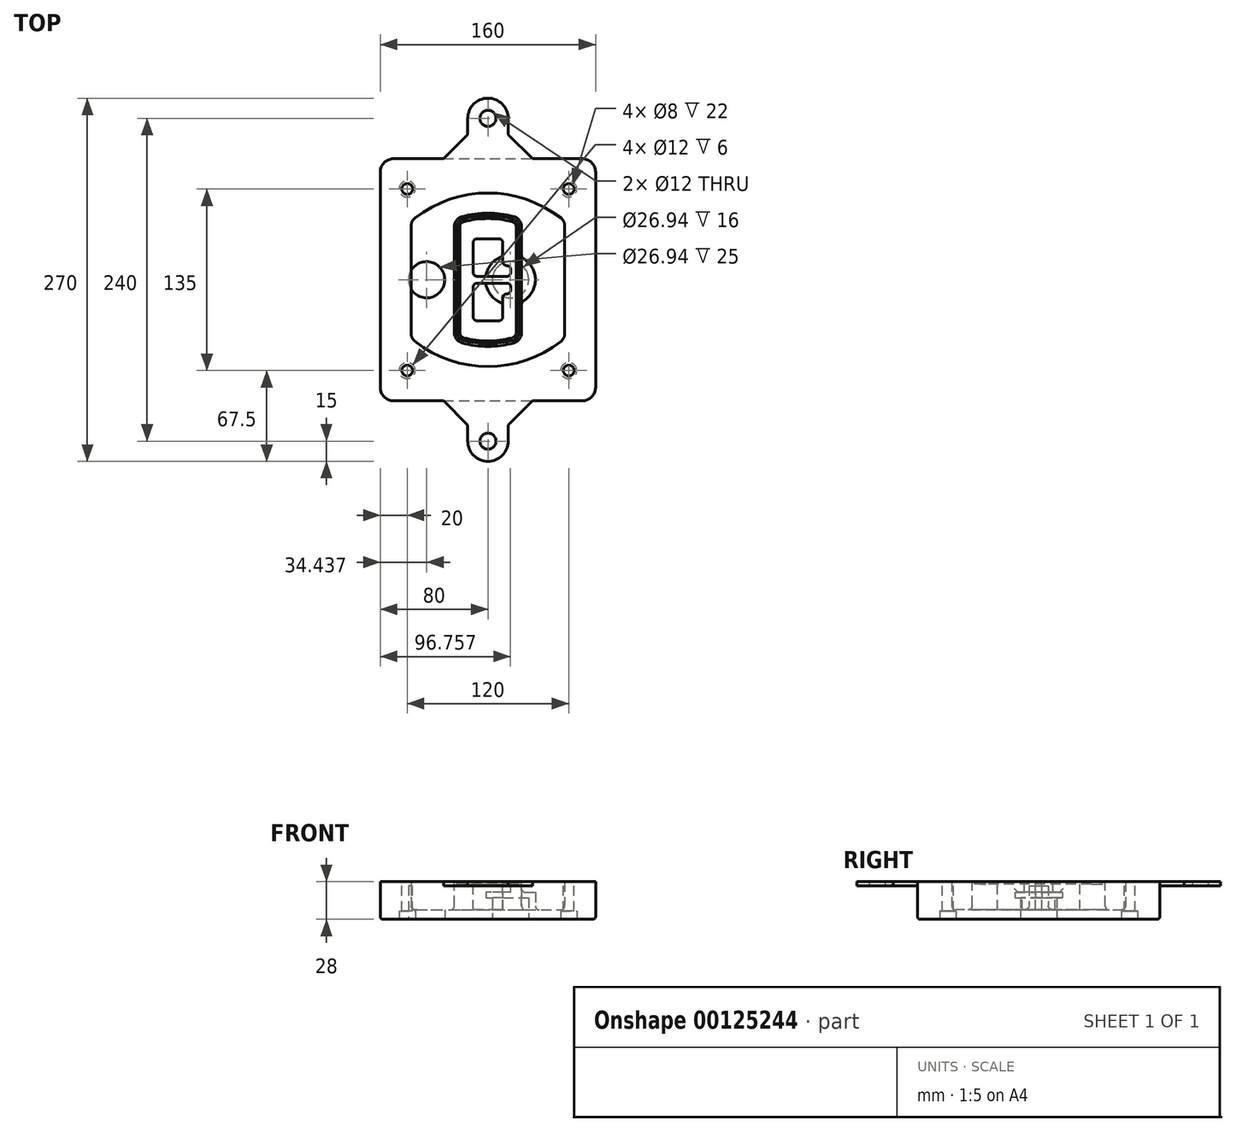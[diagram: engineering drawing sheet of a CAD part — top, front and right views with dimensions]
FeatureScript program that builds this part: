
annotation { "Feature Type Name" : "Feature", "Feature Type Description" : "" }
export const myFeature = defineFeature(function(context is Context, id is Id, definition is map)
    precondition{}
    {
        {
            var Q0;
            Q0=qCreatedBy(makeId("Top.planeOp"),FACE);
            var sketch = newSketch(context, id + "F0", { "sketchPlane" : qUnion([Q0])});
            skPoint(sketch, "E0.rect.middle", {"position": v(0, 0) * mm});
            skLineSegment(sketch, "E1.bottom", {"start": v(-70, -90) * mm, "end": v(70, -90) * mm});
            skLineSegment(sketch, "E1.top", {"start": v(-70, 90) * mm, "end": v(70, 90) * mm});
            skLineSegment(sketch, "E1.left", {"start": v(-80, -80) * mm, "end": v(-80, 80) * mm});
            skLineSegment(sketch, "E1.right", {"start": v(80, -80) * mm, "end": v(80, 80) * mm});
            skLineSegment(sketch, "E2", {"start": v(-80, 90) * mm, "end": v(80, -90) * mm, "construction": true});
            skLineSegment(sketch, "E3", {"start": v(80, 90) * mm, "end": v(-80, -90) * mm, "construction": true});
            skCircle(sketch, "E4", {"center": v(-60, 67.5) * mm, "radius": 4 * mm});
            skCircle(sketch, "E5", {"center": v(60, 67.5) * mm, "radius": 4 * mm});
            skCircle(sketch, "E6", {"center": v(60, -67.5) * mm, "radius": 4 * mm});
            skCircle(sketch, "E7", {"center": v(-60, -67.5) * mm, "radius": 4 * mm});
            skLineSegment(sketch, "E8", {"start": v(-60, 67.5) * mm, "end": v(60, 67.5) * mm, "construction": true});
            skLineSegment(sketch, "E9", {"start": v(60, 67.5) * mm, "end": v(60, -67.5) * mm, "construction": true});
            skLineSegment(sketch, "E10", {"start": v(60, -67.5) * mm, "end": v(-60, -67.5) * mm, "construction": true});
            skLineSegment(sketch, "E11", {"start": v(-60, -67.5) * mm, "end": v(-60, 67.5) * mm, "construction": true});
            skLineSegment(sketch, "E12", {"start": v(-60, 40.3) * mm, "end": v(-60, -40.3) * mm});
            skLineSegment(sketch, "E13", {"start": v(60, 40.3) * mm, "end": v(60, -40.3) * mm});
            skArc(sketch, "E14", {"start": v(56.15, 48.18) * mm, "mid": v(0, 67.5) * mm, "end": v(-56.15, 48.18) * mm});
            skArc(sketch, "E15", {"start": v(-56.15, -48.18) * mm, "mid": v(0, -67.5) * mm, "end": v(56.15, -48.18) * mm});
            skLineSegment(sketch, "E16", {"start": v(-60, 0) * mm, "end": v(60, 0) * mm, "construction": true});
            skPoint(sketch, "E17.visualSharp", {"position": v(-60, -45) * mm});
            skArc(sketch, "E17.filletArc", {"start": v(-60, -40.3) * mm, "mid": v(-58.99, -44.68) * mm, "end": v(-56.15, -48.18) * mm});
            skPoint(sketch, "E18.visualSharp", {"position": v(-60, 45) * mm});
            skArc(sketch, "E18.filletArc", {"start": v(-56.15, 48.18) * mm, "mid": v(-58.99, 44.68) * mm, "end": v(-60, 40.3) * mm});
            skPoint(sketch, "E19.visualSharp", {"position": v(60, 45) * mm});
            skArc(sketch, "E19.filletArc", {"start": v(60, 40.3) * mm, "mid": v(58.99, 44.68) * mm, "end": v(56.15, 48.18) * mm});
            skPoint(sketch, "E20.visualSharp", {"position": v(60, -45) * mm});
            skArc(sketch, "E20.filletArc", {"start": v(56.15, -48.18) * mm, "mid": v(58.99, -44.68) * mm, "end": v(60, -40.3) * mm});
            skPoint(sketch, "E21.visualSharp", {"position": v(-80, 90) * mm});
            skArc(sketch, "E21.filletArc", {"start": v(-70, 90) * mm, "mid": v(-77.07, 87.07) * mm, "end": v(-80, 80) * mm});
            skPoint(sketch, "E22.visualSharp", {"position": v(80, 90) * mm});
            skArc(sketch, "E22.filletArc", {"start": v(80, 80) * mm, "mid": v(77.07, 87.07) * mm, "end": v(70, 90) * mm});
            skPoint(sketch, "E23.visualSharp", {"position": v(80, -90) * mm});
            skArc(sketch, "E23.filletArc", {"start": v(70, -90) * mm, "mid": v(77.07, -87.07) * mm, "end": v(80, -80) * mm});
            skPoint(sketch, "E24.visualSharp", {"position": v(-80, -90) * mm});
            skArc(sketch, "E24.filletArc", {"start": v(-80, -80) * mm, "mid": v(-77.07, -87.07) * mm, "end": v(-70, -90) * mm});
            skArc(sketch, "E25.0", {"start": v(57, 40.3) * mm, "mid": v(56.3, 43.36) * mm, "end": v(54.3, 45.81) * mm});
            skLineSegment(sketch, "E25.1", {"start": v(57, 40.3) * mm, "end": v(57, -40.3) * mm});
            skArc(sketch, "E25.2", {"start": v(54.3, -45.81) * mm, "mid": v(56.3, -43.36) * mm, "end": v(57, -40.3) * mm});
            skArc(sketch, "E25.3", {"start": v(-54.3, -45.81) * mm, "mid": v(0, -64.5) * mm, "end": v(54.3, -45.81) * mm});
            skArc(sketch, "E25.4", {"start": v(-57, -40.3) * mm, "mid": v(-56.3, -43.36) * mm, "end": v(-54.3, -45.81) * mm});
            skArc(sketch, "E25.5", {"start": v(54.3, 45.81) * mm, "mid": v(0, 64.5) * mm, "end": v(-54.3, 45.81) * mm});
            skLineSegment(sketch, "E25.6", {"start": v(-57, 40.3) * mm, "end": v(-57, -40.3) * mm});
            skArc(sketch, "E25.7", {"start": v(-54.3, 45.81) * mm, "mid": v(-56.3, 43.36) * mm, "end": v(-57, 40.3) * mm});
            skArc(sketch, "E26.0", {"start": v(-58.62, 51.33) * mm, "mid": v(-62.58, 46.43) * mm, "end": v(-64, 40.3) * mm});
            skArc(sketch, "E26.1", {"start": v(58.62, 51.33) * mm, "mid": v(0, 71.5) * mm, "end": v(-58.62, 51.33) * mm});
            skArc(sketch, "E26.2", {"start": v(64, 40.3) * mm, "mid": v(62.58, 46.43) * mm, "end": v(58.62, 51.33) * mm});
            skLineSegment(sketch, "E26.3", {"start": v(64, 40.3) * mm, "end": v(64, -40.3) * mm});
            skArc(sketch, "E26.4", {"start": v(58.62, -51.33) * mm, "mid": v(62.58, -46.43) * mm, "end": v(64, -40.3) * mm});
            skLineSegment(sketch, "E26.5", {"start": v(-64, 40.3) * mm, "end": v(-64, -40.3) * mm});
            skArc(sketch, "E26.6", {"start": v(-58.62, -51.33) * mm, "mid": v(0, -71.5) * mm, "end": v(58.62, -51.33) * mm});
            skArc(sketch, "E26.7", {"start": v(-64, -40.3) * mm, "mid": v(-62.58, -46.43) * mm, "end": v(-58.62, -51.33) * mm});
            skSolve(sketch);
        }
        {
            var Q0;
            Q0=makeQuery(id+"F0.imprint","IMPRINT",FACE,{"disambiguationData":[TD([[makeQuery(id+"F0.imprint","IMPRINT",EDGE,{"derivedFrom":sQuery(id+"F0.wireOp",EDGE,"E1.bottom")}),1.0]])]});
            var Q1;
            Q1=makeQuery(id+"F0.imprint","IMPRINT",FACE,{"disambiguationData":[TD([[makeQuery(id+"F0.imprint","IMPRINT",EDGE,{"derivedFrom":sQuery(id+"F0.wireOp",EDGE,"E12")}),1.0]])]});
            var Q2;
            Q2=makeQuery(id+"F0.imprint","IMPRINT",FACE,{"disambiguationData":[TD([[makeQuery(id+"F0.imprint","IMPRINT",EDGE,{"derivedFrom":sQuery(id+"F0.wireOp",EDGE,"E25.0")}),1.0]])]});
            var Q3;
            Q3=makeQuery(id+"F0.imprint","IMPRINT",FACE,{"disambiguationData":[TD([[makeQuery(id+"F0.imprint","IMPRINT",EDGE,{"derivedFrom":sQuery(id+"F0.wireOp",EDGE,"E12")}),-1.0]])]});
            extrude(context, id + "F1", {"entities" : qUnion([Q0, Q1, Q2, Q3]), "oppositeDirection" : true, "depth" : 25 * mm});
        }
        {
            var Q0;
            Q0=makeQuery(id+"F0.imprint","IMPRINT",FACE,{"disambiguationData":[TD([[makeQuery(id+"F0.imprint","IMPRINT",EDGE,{"derivedFrom":sQuery(id+"F0.wireOp",EDGE,"E12")}),1.0]])]});
            extrude(context, id + "F2", {"entities" : qUnion([Q0]), "operationType" : NewBodyOperationType.ADD, "depth" : 3 * mm});
        }
        {
            var Q0;
            Q0=makeQuery(id+"F0.imprint","IMPRINT",FACE,{"disambiguationData":[TD([[makeQuery(id+"F0.imprint","IMPRINT",EDGE,{"derivedFrom":sQuery(id+"F0.wireOp",EDGE,"E25.0")}),1.0]])]});
            extrude(context, id + "F3", {"entities" : qUnion([Q0]), "operationType" : NewBodyOperationType.REMOVE, "oppositeDirection" : true, "depth" : 18 * mm});
        }
        {
            var Q0;
            Q0=makeQuery(id+"F2.opExtrude","CAP_FACE",FACE,{"disambiguationData":[OSD([sQuery(id+"F0.wireOp",EDGE,"E12"),sQuery(id+"F0.wireOp",EDGE,"E13"),sQuery(id+"F0.wireOp",EDGE,"E14"),sQuery(id+"F0.wireOp",EDGE,"E15"),sQuery(id+"F0.wireOp",EDGE,"E17.filletArc"),sQuery(id+"F0.wireOp",EDGE,"E18.filletArc"),sQuery(id+"F0.wireOp",EDGE,"E19.filletArc"),sQuery(id+"F0.wireOp",EDGE,"E20.filletArc"),sQuery(id+"F0.wireOp",EDGE,"E25.0"),sQuery(id+"F0.wireOp",EDGE,"E25.1"),sQuery(id+"F0.wireOp",EDGE,"E25.2"),sQuery(id+"F0.wireOp",EDGE,"E25.3"),sQuery(id+"F0.wireOp",EDGE,"E25.4"),sQuery(id+"F0.wireOp",EDGE,"E25.5"),sQuery(id+"F0.wireOp",EDGE,"E25.6"),sQuery(id+"F0.wireOp",EDGE,"E25.7")])],"isStart":false});
            var sketch = newSketch(context, id + "F4", { "sketchPlane" : qUnion([Q0])});
            skArc(sketch, "E27.0", {"start": v(-19.08, -46.97) * mm, "mid": v(0, -49.5) * mm, "end": v(19.08, -46.97) * mm});
            skArc(sketch, "E28.0", {"start": v(19.08, 46.97) * mm, "mid": v(0, 49.5) * mm, "end": v(-19.08, 46.97) * mm});
            skLineSegment(sketch, "E29", {"start": v(-25, 39.25) * mm, "end": v(-25, -39.25) * mm});
            skLineSegment(sketch, "E30", {"start": v(25, 39.25) * mm, "end": v(25, -39.25) * mm});
            skLineSegment(sketch, "E31", {"start": v(-25, 45.1) * mm, "end": v(25, 45.1) * mm, "construction": true});
            skLineSegment(sketch, "E32", {"start": v(-25, -45.1) * mm, "end": v(25, -45.1) * mm, "construction": true});
            skPoint(sketch, "E33.visualSharp", {"position": v(-25, 45.1) * mm});
            skArc(sketch, "E33.filletArc", {"start": v(-19.08, 46.97) * mm, "mid": v(-23.35, 44.11) * mm, "end": v(-25, 39.25) * mm});
            skPoint(sketch, "E34.visualSharp", {"position": v(25, 45.1) * mm});
            skArc(sketch, "E34.filletArc", {"start": v(25, 39.25) * mm, "mid": v(23.35, 44.11) * mm, "end": v(19.08, 46.97) * mm});
            skPoint(sketch, "E35.visualSharp", {"position": v(25, -45.1) * mm});
            skArc(sketch, "E35.filletArc", {"start": v(19.08, -46.97) * mm, "mid": v(23.35, -44.11) * mm, "end": v(25, -39.25) * mm});
            skPoint(sketch, "E36.visualSharp", {"position": v(-25, -45.1) * mm});
            skArc(sketch, "E36.filletArc", {"start": v(-25, -39.25) * mm, "mid": v(-23.35, -44.11) * mm, "end": v(-19.08, -46.97) * mm});
            skArc(sketch, "E37.0", {"start": v(54.3, 45.81) * mm, "mid": v(0, 64.5) * mm, "end": v(-54.3, 45.81) * mm});
            skArc(sketch, "E37.1", {"start": v(-54.3, 45.81) * mm, "mid": v(-56.3, 43.36) * mm, "end": v(-57, 40.3) * mm});
            skLineSegment(sketch, "E37.2", {"start": v(-57, 40.3) * mm, "end": v(-57, -40.3) * mm});
            skArc(sketch, "E37.3", {"start": v(-57, -40.3) * mm, "mid": v(-56.3, -43.36) * mm, "end": v(-54.3, -45.81) * mm});
            skArc(sketch, "E37.4", {"start": v(-54.3, -45.81) * mm, "mid": v(0, -64.5) * mm, "end": v(54.3, -45.81) * mm});
            skArc(sketch, "E37.5", {"start": v(54.3, -45.81) * mm, "mid": v(56.3, -43.36) * mm, "end": v(57, -40.3) * mm});
            skLineSegment(sketch, "E37.6", {"start": v(57, 40.3) * mm, "end": v(57, -40.3) * mm});
            skArc(sketch, "E37.7", {"start": v(57, 40.3) * mm, "mid": v(56.3, 43.36) * mm, "end": v(54.3, 45.81) * mm});
            skLineSegment(sketch, "E38.0", {"start": v(23, 39.25) * mm, "end": v(23, -39.25) * mm});
            skArc(sketch, "E38.1", {"start": v(18.56, -45.04) * mm, "mid": v(21.76, -42.9) * mm, "end": v(23, -39.25) * mm});
            skArc(sketch, "E38.2", {"start": v(-18.56, -45.04) * mm, "mid": v(0, -47.5) * mm, "end": v(18.56, -45.04) * mm});
            skArc(sketch, "E38.3", {"start": v(-23, -39.25) * mm, "mid": v(-21.76, -42.9) * mm, "end": v(-18.56, -45.04) * mm});
            skLineSegment(sketch, "E38.4", {"start": v(-23, 39.25) * mm, "end": v(-23, -39.25) * mm});
            skArc(sketch, "E38.5", {"start": v(23, 39.25) * mm, "mid": v(21.76, 42.9) * mm, "end": v(18.56, 45.04) * mm});
            skArc(sketch, "E38.6", {"start": v(-18.56, 45.04) * mm, "mid": v(-21.76, 42.9) * mm, "end": v(-23, 39.25) * mm});
            skArc(sketch, "E38.7", {"start": v(18.56, 45.04) * mm, "mid": v(0, 47.5) * mm, "end": v(-18.56, 45.04) * mm});
            skArc(sketch, "E39.0", {"start": v(21, 39.25) * mm, "mid": v(20.18, 41.68) * mm, "end": v(18.04, 43.1) * mm});
            skLineSegment(sketch, "E39.1", {"start": v(21, 39.25) * mm, "end": v(21, -39.25) * mm});
            skArc(sketch, "E39.2", {"start": v(18.04, -43.1) * mm, "mid": v(20.18, -41.68) * mm, "end": v(21, -39.25) * mm});
            skArc(sketch, "E39.3", {"start": v(-18.04, -43.1) * mm, "mid": v(0, -45.5) * mm, "end": v(18.04, -43.1) * mm});
            skArc(sketch, "E39.4", {"start": v(-21, -39.25) * mm, "mid": v(-20.18, -41.68) * mm, "end": v(-18.04, -43.1) * mm});
            skArc(sketch, "E39.5", {"start": v(18.04, 43.1) * mm, "mid": v(0, 45.5) * mm, "end": v(-18.04, 43.1) * mm});
            skLineSegment(sketch, "E39.6", {"start": v(-21, 39.25) * mm, "end": v(-21, -39.25) * mm});
            skArc(sketch, "E39.7", {"start": v(-18.04, 43.1) * mm, "mid": v(-20.18, 41.68) * mm, "end": v(-21, 39.25) * mm});
            skLineSegment(sketch, "E40", {"start": v(-25, 0) * mm, "end": v(25, 0) * mm, "construction": true});
            skLineSegment(sketch, "E41", {"start": v(-11, 5.5) * mm, "end": v(-11, 27.5) * mm});
            skLineSegment(sketch, "E42", {"start": v(-8, 30.5) * mm, "end": v(8, 30.5) * mm});
            skLineSegment(sketch, "E43", {"start": v(11, 27.5) * mm, "end": v(11, 13.5) * mm});
            skLineSegment(sketch, "E44", {"start": v(14, 10.5) * mm, "end": v(14, 10.5) * mm});
            skLineSegment(sketch, "E45", {"start": v(17, 7.5) * mm, "end": v(17, 5.5) * mm});
            skLineSegment(sketch, "E46", {"start": v(14, 2.5) * mm, "end": v(-8, 2.5) * mm});
            skPoint(sketch, "E47.visualSharp", {"position": v(-11, 30.5) * mm});
            skArc(sketch, "E47.filletArc", {"start": v(-8, 30.5) * mm, "mid": v(-10.12, 29.62) * mm, "end": v(-11, 27.5) * mm});
            skPoint(sketch, "E48.visualSharp", {"position": v(11, 30.5) * mm});
            skArc(sketch, "E48.filletArc", {"start": v(11, 27.5) * mm, "mid": v(10.12, 29.62) * mm, "end": v(8, 30.5) * mm});
            skPoint(sketch, "E49.visualSharp", {"position": v(11, 10.5) * mm});
            skArc(sketch, "E49.filletArc", {"start": v(11, 13.5) * mm, "mid": v(11.88, 11.38) * mm, "end": v(14, 10.5) * mm});
            skPoint(sketch, "E50.visualSharp", {"position": v(17, 10.5) * mm});
            skArc(sketch, "E50.filletArc", {"start": v(17, 7.5) * mm, "mid": v(16.12, 9.62) * mm, "end": v(14, 10.5) * mm});
            skPoint(sketch, "E51.visualSharp", {"position": v(17, 2.5) * mm});
            skArc(sketch, "E51.filletArc", {"start": v(14, 2.5) * mm, "mid": v(16.12, 3.38) * mm, "end": v(17, 5.5) * mm});
            skPoint(sketch, "E52.visualSharp", {"position": v(-11, 2.5) * mm});
            skArc(sketch, "E52.filletArc", {"start": v(-11, 5.5) * mm, "mid": v(-10.12, 3.38) * mm, "end": v(-8, 2.5) * mm});
            skLineSegment(sketch, "E53.0.MirrorCS", {"start": v(14, -2.5) * mm, "end": v(-8, -2.5) * mm});
            skArc(sketch, "E54.0.MirrorCS", {"start": v(-11, -5.5) * mm, "mid": v(-10.12, -3.38) * mm, "end": v(-8, -2.5) * mm});
            skLineSegment(sketch, "E55.0.MirrorCS", {"start": v(-11, -5.5) * mm, "end": v(-11, -27.5) * mm});
            skArc(sketch, "E56.0.MirrorCS", {"start": v(-8, -30.5) * mm, "mid": v(-10.12, -29.62) * mm, "end": v(-11, -27.5) * mm});
            skLineSegment(sketch, "E57.0.MirrorCS", {"start": v(-8, -30.5) * mm, "end": v(8, -30.5) * mm});
            skArc(sketch, "E58.0.MirrorCS", {"start": v(11, -27.5) * mm, "mid": v(10.12, -29.62) * mm, "end": v(8, -30.5) * mm});
            skLineSegment(sketch, "E59.0.MirrorCS", {"start": v(11, -27.5) * mm, "end": v(11, -13.5) * mm});
            skArc(sketch, "E60.0.MirrorCS", {"start": v(11, -13.5) * mm, "mid": v(11.88, -11.38) * mm, "end": v(14, -10.5) * mm});
            skArc(sketch, "E61.0.MirrorCS", {"start": v(17, -7.5) * mm, "mid": v(16.12, -9.62) * mm, "end": v(14, -10.5) * mm});
            skLineSegment(sketch, "E62.0.MirrorCS", {"start": v(17, -7.5) * mm, "end": v(17, -5.5) * mm});
            skArc(sketch, "E63.0.MirrorCS", {"start": v(14, -2.5) * mm, "mid": v(16.12, -3.38) * mm, "end": v(17, -5.5) * mm});
            skSolve(sketch);
        }
        {
            var Q0;
            Q0=makeQuery(id+"F4.imprint","IMPRINT",FACE,{"disambiguationData":[TD([[makeQuery(id+"F4.imprint","IMPRINT",EDGE,{"derivedFrom":sQuery(id+"F4.wireOp",EDGE,"E27.0")}),1.0]])]});
            var Q1;
            Q1=makeQuery(id+"F4.imprint","IMPRINT",FACE,{"disambiguationData":[TD([[makeQuery(id+"F4.imprint","IMPRINT",EDGE,{"derivedFrom":sQuery(id+"F4.wireOp",EDGE,"E38.0")}),-1.0]])]});
            var Q2;
            Q2=makeQuery(id+"F4.imprint","IMPRINT",FACE,{"disambiguationData":[TD([[makeQuery(id+"F4.imprint","IMPRINT",EDGE,{"derivedFrom":sQuery(id+"F4.wireOp",EDGE,"E39.0")}),1.0]])]});
            extrude(context, id + "F5", {"entities" : qUnion([Q0, Q1, Q2]), "operationType" : NewBodyOperationType.ADD, "endBound" : BoundingType.UP_TO_NEXT, "oppositeDirection" : true, "depth" : 25 * mm});
        }
        {
            var Q0;
            Q0=makeQuery(id+"F4.imprint","IMPRINT",FACE,{"disambiguationData":[TD([[makeQuery(id+"F4.imprint","IMPRINT",EDGE,{"derivedFrom":sQuery(id+"F4.wireOp",EDGE,"E38.0")}),-1.0]])]});
            extrude(context, id + "F6", {"entities" : qUnion([Q0]), "operationType" : NewBodyOperationType.REMOVE, "oppositeDirection" : true, "depth" : 2 * mm});
        }
        {
            var Q0;
            Q0=makeQuery(id+"F1.opExtrude","CAP_FACE",FACE,{"disambiguationData":[OSD([sQuery(id+"F0.wireOp",EDGE,"E1.bottom"),sQuery(id+"F0.wireOp",EDGE,"E1.top"),sQuery(id+"F0.wireOp",EDGE,"E1.left"),sQuery(id+"F0.wireOp",EDGE,"E1.right"),sQuery(id+"F0.wireOp",EDGE,"E4"),sQuery(id+"F0.wireOp",EDGE,"E5"),sQuery(id+"F0.wireOp",EDGE,"E6"),sQuery(id+"F0.wireOp",EDGE,"E7"),sQuery(id+"F0.wireOp",EDGE,"E21.filletArc"),sQuery(id+"F0.wireOp",EDGE,"E22.filletArc"),sQuery(id+"F0.wireOp",EDGE,"E23.filletArc"),sQuery(id+"F0.wireOp",EDGE,"E24.filletArc")])],"isStart":false});
            var sketch = newSketch(context, id + "F7", { "sketchPlane" : qUnion([Q0])});
            skCircle(sketch, "E64", {"center": v(16.76, 0) * mm, "radius": 13.47 * mm});
            skCircle(sketch, "E65", {"center": v(-45.56, 0) * mm, "radius": 13.47 * mm});
            skLineSegment(sketch, "E66", {"start": v(80, 0) * mm, "end": v(-80, 0) * mm});
            skCircle(sketch, "E67", {"center": v(16.76, 0) * mm, "radius": 18.47 * mm});
            skCircle(sketch, "E68", {"center": v(60, -67.5) * mm, "radius": 6 * mm});
            skCircle(sketch, "E69", {"center": v(-60, -67.5) * mm, "radius": 6 * mm});
            skCircle(sketch, "E70", {"center": v(-60, 67.5) * mm, "radius": 6 * mm});
            skCircle(sketch, "E71", {"center": v(60, 67.5) * mm, "radius": 6 * mm});
            skSolve(sketch);
        }
        {
            var Q0;
            {var subQ1=sQuery(id+"F7.wireOp",EDGE,"E66");var subQ4=sQuery(id+"F7.wireOp",EDGE,"E64");var subQ6=makeQuery(id+"F7.imprint","INTERSECT",VERTEX,{"disambiguationData":[OD(0.0)],"derivedFrom":[subQ4,subQ1]});Q0=makeQuery(id+"F7.imprint","IMPRINT",FACE,{"disambiguationData":[TD([[makeQuery(id+"F7.imprint","IMPRINT",EDGE,{"disambiguationData":[TD([[subQ6,-1.0]])],"derivedFrom":subQ4}),-1.0]])]});}
            var Q1;
            {var subQ0=sQuery(id+"F7.wireOp",EDGE,"E66");var subQ1=sQuery(id+"F7.wireOp",EDGE,"E64");var subQ3=makeQuery(id+"F7.imprint","INTERSECT",VERTEX,{"disambiguationData":[OD(0.0)],"derivedFrom":[subQ1,subQ0]});Q1=makeQuery(id+"F7.imprint","IMPRINT",FACE,{"disambiguationData":[TD([[makeQuery(id+"F7.imprint","IMPRINT",EDGE,{"disambiguationData":[TD([[subQ3,-1.0]])],"derivedFrom":subQ1}),1.0]])]});}
            var Q2;
            {var subQ0=sQuery(id+"F7.wireOp",EDGE,"E66");var subQ1=sQuery(id+"F7.wireOp",EDGE,"E64");var subQ3=makeQuery(id+"F7.imprint","INTERSECT",VERTEX,{"disambiguationData":[OD(0.0)],"derivedFrom":[subQ1,subQ0]});Q2=makeQuery(id+"F7.imprint","IMPRINT",FACE,{"disambiguationData":[TD([[makeQuery(id+"F7.imprint","IMPRINT",EDGE,{"disambiguationData":[TD([[subQ3,1.0]])],"derivedFrom":subQ1}),1.0]])]});}
            var Q3;
            {var subQ1=sQuery(id+"F7.wireOp",EDGE,"E66");var subQ4=sQuery(id+"F7.wireOp",EDGE,"E64");var subQ6=makeQuery(id+"F7.imprint","INTERSECT",VERTEX,{"disambiguationData":[OD(0.0)],"derivedFrom":[subQ4,subQ1]});Q3=makeQuery(id+"F7.imprint","IMPRINT",FACE,{"disambiguationData":[TD([[makeQuery(id+"F7.imprint","IMPRINT",EDGE,{"disambiguationData":[TD([[subQ6,1.0]])],"derivedFrom":subQ4}),-1.0]])]});}
            extrude(context, id + "F8", {"entities" : qUnion([Q0, Q1, Q2, Q3]), "operationType" : NewBodyOperationType.ADD, "oppositeDirection" : true, "depth" : 20 * mm});
        }
        {
            var Q0;
            {var subQ0=sQuery(id+"F7.wireOp",EDGE,"E66");var subQ1=sQuery(id+"F7.wireOp",EDGE,"E64");var subQ3=makeQuery(id+"F7.imprint","INTERSECT",VERTEX,{"disambiguationData":[OD(0.0)],"derivedFrom":[subQ1,subQ0]});Q0=makeQuery(id+"F7.imprint","IMPRINT",FACE,{"disambiguationData":[TD([[makeQuery(id+"F7.imprint","IMPRINT",EDGE,{"disambiguationData":[TD([[subQ3,-1.0]])],"derivedFrom":subQ1}),1.0]])]});}
            var Q1;
            {var subQ0=sQuery(id+"F7.wireOp",EDGE,"E66");var subQ1=sQuery(id+"F7.wireOp",EDGE,"E64");var subQ3=makeQuery(id+"F7.imprint","INTERSECT",VERTEX,{"disambiguationData":[OD(0.0)],"derivedFrom":[subQ1,subQ0]});Q1=makeQuery(id+"F7.imprint","IMPRINT",FACE,{"disambiguationData":[TD([[makeQuery(id+"F7.imprint","IMPRINT",EDGE,{"disambiguationData":[TD([[subQ3,1.0]])],"derivedFrom":subQ1}),1.0]])]});}
            extrude(context, id + "F9", {"entities" : qUnion([Q0, Q1]), "operationType" : NewBodyOperationType.REMOVE, "oppositeDirection" : true, "depth" : 16 * mm});
        }
        {
            var Q0;
            {var subQ0=sQuery(id+"F7.wireOp",EDGE,"E66");var subQ1=sQuery(id+"F7.wireOp",EDGE,"E65");var subQ3=makeQuery(id+"F7.imprint","INTERSECT",VERTEX,{"disambiguationData":[OD(0.0)],"derivedFrom":[subQ1,subQ0]});Q0=makeQuery(id+"F7.imprint","IMPRINT",FACE,{"disambiguationData":[TD([[makeQuery(id+"F7.imprint","IMPRINT",EDGE,{"disambiguationData":[TD([[subQ3,-1.0]])],"derivedFrom":subQ1}),1.0]])]});}
            var Q1;
            {var subQ0=sQuery(id+"F7.wireOp",EDGE,"E66");var subQ1=sQuery(id+"F7.wireOp",EDGE,"E65");var subQ3=makeQuery(id+"F7.imprint","INTERSECT",VERTEX,{"disambiguationData":[OD(0.0)],"derivedFrom":[subQ1,subQ0]});Q1=makeQuery(id+"F7.imprint","IMPRINT",FACE,{"disambiguationData":[TD([[makeQuery(id+"F7.imprint","IMPRINT",EDGE,{"disambiguationData":[TD([[subQ3,1.0]])],"derivedFrom":subQ1}),1.0]])]});}
            extrude(context, id + "F10", {"entities" : qUnion([Q0, Q1]), "operationType" : NewBodyOperationType.REMOVE, "oppositeDirection" : true, "depth" : 25 * mm});
        }
        {
            var Q0;
            Q0=makeQuery(id+"F7.imprint","IMPRINT",FACE,{"disambiguationData":[TD([[makeQuery(id+"F7.imprint","IMPRINT",EDGE,{"derivedFrom":sQuery(id+"F7.wireOp",EDGE,"E68")}),1.0]])]});
            var Q1;
            Q1=makeQuery(id+"F7.imprint","IMPRINT",FACE,{"disambiguationData":[TD([[makeQuery(id+"F7.imprint","IMPRINT",EDGE,{"derivedFrom":makeQuery(id+"F1.opExtrude","CAP_EDGE",EDGE,{"disambiguationData":[OSD([sQuery(id+"F0.wireOp",EDGE,"E5")])],"isStart":false})}),-1.0]])]});
            var Q2;
            Q2=makeQuery(id+"F7.imprint","IMPRINT",FACE,{"disambiguationData":[TD([[makeQuery(id+"F7.imprint","IMPRINT",EDGE,{"derivedFrom":sQuery(id+"F7.wireOp",EDGE,"E69")}),1.0]])]});
            var Q3;
            Q3=makeQuery(id+"F7.imprint","IMPRINT",FACE,{"disambiguationData":[TD([[makeQuery(id+"F7.imprint","IMPRINT",EDGE,{"derivedFrom":makeQuery(id+"F1.opExtrude","CAP_EDGE",EDGE,{"disambiguationData":[OSD([sQuery(id+"F0.wireOp",EDGE,"E4")])],"isStart":false})}),-1.0]])]});
            var Q4;
            Q4=makeQuery(id+"F7.imprint","IMPRINT",FACE,{"disambiguationData":[TD([[makeQuery(id+"F7.imprint","IMPRINT",EDGE,{"derivedFrom":sQuery(id+"F7.wireOp",EDGE,"E70")}),1.0]])]});
            var Q5;
            Q5=makeQuery(id+"F7.imprint","IMPRINT",FACE,{"disambiguationData":[TD([[makeQuery(id+"F7.imprint","IMPRINT",EDGE,{"derivedFrom":makeQuery(id+"F1.opExtrude","CAP_EDGE",EDGE,{"disambiguationData":[OSD([sQuery(id+"F0.wireOp",EDGE,"E7")])],"isStart":false})}),-1.0]])]});
            var Q6;
            Q6=makeQuery(id+"F7.imprint","IMPRINT",FACE,{"disambiguationData":[TD([[makeQuery(id+"F7.imprint","IMPRINT",EDGE,{"derivedFrom":sQuery(id+"F7.wireOp",EDGE,"E71")}),1.0]])]});
            var Q7;
            Q7=makeQuery(id+"F7.imprint","IMPRINT",FACE,{"disambiguationData":[TD([[makeQuery(id+"F7.imprint","IMPRINT",EDGE,{"derivedFrom":makeQuery(id+"F1.opExtrude","CAP_EDGE",EDGE,{"disambiguationData":[OSD([sQuery(id+"F0.wireOp",EDGE,"E6")])],"isStart":false})}),-1.0]])]});
            extrude(context, id + "F11", {"entities" : qUnion([Q0, Q1, Q2, Q3, Q4, Q5, Q6, Q7]), "operationType" : NewBodyOperationType.REMOVE, "oppositeDirection" : true, "depth" : 6 * mm});
        }
        {
            var Q0;
            Q0=makeQuery(id+"F9.boolean.opBoolean","COPY",FACE,{"derivedFrom":makeQuery(id+"F9.opExtrude","CAP_FACE",FACE,{"disambiguationData":[OSD([sQuery(id+"F7.wireOp",EDGE,"E64")])],"isStart":false})});
            var sketch = newSketch(context, id + "F12", { "sketchPlane" : qUnion([Q0])});
            skArc(sketch, "E72.0", {"start": v(11, 17.55) * mm, "mid": v(2.57, 11.82) * mm, "end": v(-1.54, 2.5) * mm});
            skArc(sketch, "E72.1", {"start": v(-1.54, -2.5) * mm, "mid": v(2.57, -11.82) * mm, "end": v(11, -17.55) * mm});
            skLineSegment(sketch, "E73", {"start": v(-1.54, -2.5) * mm, "end": v(14, -2.5) * mm});
            skLineSegment(sketch, "E74.0", {"start": v(14, 2.5) * mm, "end": v(-1.54, 2.5) * mm});
            skArc(sketch, "E74.1", {"start": v(14, 2.5) * mm, "mid": v(16.12, 3.38) * mm, "end": v(17, 5.5) * mm});
            skLineSegment(sketch, "E74.2", {"start": v(17, 7.5) * mm, "end": v(17, 5.5) * mm});
            skArc(sketch, "E74.3", {"start": v(17, 7.5) * mm, "mid": v(16.12, 9.62) * mm, "end": v(14, 10.5) * mm});
            skArc(sketch, "E74.4", {"start": v(11, 13.5) * mm, "mid": v(11.88, 11.38) * mm, "end": v(14, 10.5) * mm});
            skLineSegment(sketch, "E74.5", {"start": v(11, 17.55) * mm, "end": v(11, 13.5) * mm});
            skLineSegment(sketch, "E74.7", {"start": v(14, -2.5) * mm, "end": v(-1.54, -2.5) * mm});
            skArc(sketch, "E74.8", {"start": v(14, -2.5) * mm, "mid": v(16.12, -3.38) * mm, "end": v(17, -5.5) * mm});
            skLineSegment(sketch, "E74.9", {"start": v(17, -7.5) * mm, "end": v(17, -5.5) * mm});
            skArc(sketch, "E74.10", {"start": v(17, -7.5) * mm, "mid": v(16.12, -9.62) * mm, "end": v(14, -10.5) * mm});
            skArc(sketch, "E74.11", {"start": v(11, -13.5) * mm, "mid": v(11.88, -11.38) * mm, "end": v(14, -10.5) * mm});
            skLineSegment(sketch, "E74.12", {"start": v(11, -17.55) * mm, "end": v(11, -13.5) * mm});
            skPoint(sketch, "E75.orphan", {"position": v(11, -27.5) * mm});
            skPoint(sketch, "E76.orphan", {"position": v(-8, -2.5) * mm});
            skPoint(sketch, "E77.orphan", {"position": v(-8, 2.5) * mm});
            skPoint(sketch, "E78.orphan", {"position": v(11, 27.5) * mm});
            skSolve(sketch);
        }
        {
            var Q0;
            {var subQ7=sQuery(id+"F12.wireOp",EDGE,"E72.0");var subQ14=sQuery(id+"F12.wireOp",EDGE,"E72.1");var subQ16=sQuery(id+"F12.wireOp",EDGE,"E74.1");var subQ18=sQuery(id+"F12.wireOp",EDGE,"E74.8");Q0=qUnion([makeQuery(id+"F12.imprint","IMPRINT",FACE,{"disambiguationData":[TD([[makeQuery(id+"F12.imprint","IMPRINT",EDGE,{"derivedFrom":subQ7}),1.0]])]}),makeQuery(id+"F12.imprint","IMPRINT",FACE,{"disambiguationData":[TD([[makeQuery(id+"F12.imprint","IMPRINT",EDGE,{"derivedFrom":subQ14}),1.0]])]}),makeQuery(id+"F12.imprint","IMPRINT",FACE,{"disambiguationData":[TD([[makeQuery(id+"F12.imprint","IMPRINT",EDGE,{"derivedFrom":subQ16}),1.0]])]}),makeQuery(id+"F12.imprint","IMPRINT",FACE,{"disambiguationData":[TD([[makeQuery(id+"F12.imprint","IMPRINT",EDGE,{"derivedFrom":subQ18}),-1.0]])]})]);}
            var Q1;
            Q1=makeQuery(id+"F5.boolean.opBoolean","SPLIT",FACE,{"disambiguationData":[TD([makeQuery(id+"F5.opExtrude","SWEPT_FACE",FACE,{"disambiguationData":[OSD([sQuery(id+"F4.wireOp",EDGE,"E41")])]})])],"derivedFrom":makeQuery(id+"F3.boolean.opBoolean","COPY",FACE,{"derivedFrom":makeQuery(id+"F3.opExtrude","CAP_FACE",FACE,{"disambiguationData":[OSD([sQuery(id+"F0.wireOp",EDGE,"E25.0"),sQuery(id+"F0.wireOp",EDGE,"E25.1"),sQuery(id+"F0.wireOp",EDGE,"E25.2"),sQuery(id+"F0.wireOp",EDGE,"E25.3"),sQuery(id+"F0.wireOp",EDGE,"E25.4"),sQuery(id+"F0.wireOp",EDGE,"E25.5"),sQuery(id+"F0.wireOp",EDGE,"E25.6"),sQuery(id+"F0.wireOp",EDGE,"E25.7")])],"isStart":false})})});
            extrude(context, id + "F13", {"entities" : qUnion([Q0]), "operationType" : NewBodyOperationType.REMOVE, "endBound" : BoundingType.UP_TO_SURFACE, "endBoundEntityFace" : qUnion([Q1]), "depth" : 25 * mm});
        }
        {
            var Q0;
            Q0=makeQuery(id+"F3.boolean.opBoolean","COPY",EDGE,{"derivedFrom":makeQuery(id+"F3.opExtrude","CAP_EDGE",EDGE,{"disambiguationData":[OSD([sQuery(id+"F0.wireOp",EDGE,"E25.6")])],"isStart":false})});
            var Q1;
            Q1=makeQuery(id+"F8.boolean.opBoolean","INTERSECT",EDGE,{"derivedFrom":[makeQuery(id+"F5.opExtrude","SWEPT_FACE",FACE,{"disambiguationData":[OSD([sQuery(id+"F4.wireOp",EDGE,"E30")])]}),makeQuery(id+"F8.opExtrude","CAP_FACE",FACE,{"disambiguationData":[OSD([sQuery(id+"F7.wireOp",EDGE,"E67")])],"isStart":false})]});
            var Q2;
            Q2=makeQuery(id+"F8.boolean.opBoolean","INTERSECT",EDGE,{"disambiguationData":[OD(1.0)],"derivedFrom":[makeQuery(id+"F5.opExtrude","SWEPT_FACE",FACE,{"disambiguationData":[OSD([sQuery(id+"F4.wireOp",EDGE,"E30")])]}),makeQuery(id+"F8.opExtrude","SWEPT_FACE",FACE,{"disambiguationData":[OSD([sQuery(id+"F7.wireOp",EDGE,"E67")])]})]});
            var Q3;
            {var subQ0=sQuery(id+"F4.wireOp",EDGE,"E30");Q3=makeQuery(id+"F8.boolean.opBoolean","SPLIT",EDGE,{"disambiguationData":[TD([makeQuery(id+"F5.opExtrude","SWEPT_FACE",FACE,{"disambiguationData":[OSD([sQuery(id+"F4.wireOp",EDGE,"E35.filletArc")])]})])],"derivedFrom":makeQuery(id+"F5.opExtrude","CAP_EDGE",EDGE,{"disambiguationData":[OSD([subQ0])],"isStart":false})});}
            var Q4;
            {var subQ0=sQuery(id+"F0.wireOp",EDGE,"E25.7");var subQ1=sQuery(id+"F0.wireOp",EDGE,"E25.1");var subQ2=sQuery(id+"F0.wireOp",EDGE,"E25.6");var subQ3=sQuery(id+"F0.wireOp",EDGE,"E25.5");var subQ4=sQuery(id+"F0.wireOp",EDGE,"E25.4");var subQ5=sQuery(id+"F0.wireOp",EDGE,"E25.0");var subQ6=sQuery(id+"F0.wireOp",EDGE,"E25.2");var subQ7=sQuery(id+"F0.wireOp",EDGE,"E25.3");Q4=makeQuery(id+"F8.boolean.opBoolean","INTERSECT",EDGE,{"derivedFrom":[makeQuery(id+"F5.boolean.opBoolean","SPLIT",FACE,{"disambiguationData":[TD([makeQuery(id+"F2.opExtrude","SWEPT_FACE",FACE,{"disambiguationData":[OSD([subQ5])]})])],"derivedFrom":makeQuery(id+"F3.boolean.opBoolean","COPY",FACE,{"derivedFrom":makeQuery(id+"F3.opExtrude","CAP_FACE",FACE,{"disambiguationData":[OSD([subQ5,subQ1,subQ6,subQ7,subQ4,subQ3,subQ2,subQ0])],"isStart":false})})}),makeQuery(id+"F8.opExtrude","SWEPT_FACE",FACE,{"disambiguationData":[OSD([sQuery(id+"F7.wireOp",EDGE,"E67")])]})]});}
            var Q5;
            Q5=makeQuery(id+"F8.boolean.opBoolean","INTERSECT",EDGE,{"disambiguationData":[OD(0.0)],"derivedFrom":[makeQuery(id+"F5.opExtrude","SWEPT_FACE",FACE,{"disambiguationData":[OSD([sQuery(id+"F4.wireOp",EDGE,"E30")])]}),makeQuery(id+"F8.opExtrude","SWEPT_FACE",FACE,{"disambiguationData":[OSD([sQuery(id+"F7.wireOp",EDGE,"E67")])]})]});
            fillet(context, id + "F14", {"entities" : qUnion([Q0, Q1, Q2, Q3, Q4, Q5]), "radius" : 3 * mm, "tangentPropagation" : true, "allowEdgeOverflow" : false});
        }
        {
            var Q0;
            Q0=makeQuery(id+"F1.opExtrude","CAP_EDGE",EDGE,{"disambiguationData":[OSD([sQuery(id+"F0.wireOp",EDGE,"E1.bottom")])],"isStart":false});
            fillet(context, id + "F15", {"entities" : qUnion([Q0]), "radius" : 2 * mm, "tangentPropagation" : true, "allowEdgeOverflow" : false});
        }
        {
            var Q0;
            {var subQ0=sQuery(id+"F0.wireOp",EDGE,"E22.filletArc");var subQ1=sQuery(id+"F0.wireOp",EDGE,"E7");var subQ2=sQuery(id+"F0.wireOp",EDGE,"E6");var subQ3=sQuery(id+"F0.wireOp",EDGE,"E5");var subQ4=sQuery(id+"F0.wireOp",EDGE,"E4");var subQ5=sQuery(id+"F0.wireOp",EDGE,"E1.bottom");var subQ6=sQuery(id+"F0.wireOp",EDGE,"E21.filletArc");var subQ7=sQuery(id+"F0.wireOp",EDGE,"E1.top");var subQ8=sQuery(id+"F0.wireOp",EDGE,"E1.left");var subQ9=sQuery(id+"F0.wireOp",EDGE,"E1.right");var subQ10=sQuery(id+"F0.wireOp",EDGE,"E23.filletArc");var subQ11=sQuery(id+"F0.wireOp",EDGE,"E24.filletArc");Q0=makeQuery(id+"F2.boolean.opBoolean","SPLIT",FACE,{"disambiguationData":[TD([makeQuery(id+"F1.opExtrude","SWEPT_FACE",FACE,{"disambiguationData":[OSD([subQ5])]})])],"derivedFrom":makeQuery(id+"F1.opExtrude","CAP_FACE",FACE,{"disambiguationData":[OSD([subQ5,subQ7,subQ8,subQ9,subQ4,subQ3,subQ2,subQ1,subQ6,subQ0,subQ10,subQ11])],"isStart":true})});}
            var sketch = newSketch(context, id + "F16", { "sketchPlane" : qUnion([Q0])});
            skLineSegment(sketch, "E79", {"start": v(0, 0) * mm, "end": v(0, 120) * mm, "construction": true});
            skPoint(sketch, "E79.endSnap0", {"position": v(0, 90) * mm});
            skLineSegment(sketch, "E80", {"start": v(0, 120) * mm, "end": v(0, -119.46) * mm, "construction": true});
            skPoint(sketch, "E80.endSnap0", {"position": v(0, -67.5) * mm});
            skLineSegment(sketch, "E81", {"start": v(0, -119.46) * mm, "end": v(0, 0) * mm, "construction": true});
            skLineSegment(sketch, "E82", {"start": v(0, 0) * mm, "end": v(-127.73, 0) * mm, "construction": true});
            skPoint(sketch, "E82.endSnap0", {"position": v(-80, 0) * mm});
            skLineSegment(sketch, "E83", {"start": v(-127.73, 0) * mm, "end": v(120.45, 0) * mm, "construction": true});
            skArc(sketch, "E84", {"start": v(15, 120) * mm, "mid": v(0, 135) * mm, "end": v(-15, 120) * mm});
            skLineSegment(sketch, "E85", {"start": v(-15, 120) * mm, "end": v(-15, 108) * mm});
            skLineSegment(sketch, "E86", {"start": v(15, 120) * mm, "end": v(15, 108) * mm});
            skLineSegment(sketch, "E87", {"start": v(15, 108) * mm, "end": v(33, 90) * mm});
            skCircle(sketch, "E88", {"center": v(0, 120) * mm, "radius": 6 * mm});
            skLineSegment(sketch, "E89", {"start": v(-15, 108) * mm, "end": v(-33, 90) * mm});
            skLineSegment(sketch, "E90.MirrorCS", {"start": v(15, -120) * mm, "end": v(15, -108) * mm});
            skArc(sketch, "E91.MirrorCS", {"start": v(15, -120) * mm, "mid": v(0, -135) * mm, "end": v(-15, -120) * mm});
            skLineSegment(sketch, "E92.MirrorCS", {"start": v(-15, -120) * mm, "end": v(-15, -108) * mm});
            skLineSegment(sketch, "E93.MirrorCS", {"start": v(-15, -108) * mm, "end": v(-33, -90) * mm});
            skLineSegment(sketch, "E94.MirrorCS", {"start": v(15, -108) * mm, "end": v(33, -90) * mm});
            skCircle(sketch, "E95.MirrorC", {"center": v(0, -120) * mm, "radius": 6 * mm});
            skSolve(sketch);
        }
        {
            var Q0;
            Q0=makeQuery(id+"F16.imprint","IMPRINT",FACE,{"disambiguationData":[TD([[makeQuery(id+"F16.imprint","IMPRINT",EDGE,{"derivedFrom":sQuery(id+"F16.wireOp",EDGE,"E84")}),1.0]])]});
            var Q1;
            Q1=makeQuery(id+"F16.imprint","IMPRINT",FACE,{"disambiguationData":[TD([[makeQuery(id+"F16.imprint","IMPRINT",EDGE,{"derivedFrom":sQuery(id+"F16.wireOp",EDGE,"E90.MirrorCS")}),1.0]])]});
            var Q2;
            Q2=makeQuery(id+"F16.imprint","IMPRINT",FACE,{"disambiguationData":[TD([[makeQuery(id+"F16.imprint","IMPRINT",EDGE,{"derivedFrom":makeQuery(id+"F1.opExtrude","CAP_EDGE",EDGE,{"disambiguationData":[OSD([sQuery(id+"F0.wireOp",EDGE,"E1.left")])],"isStart":true})}),-1.0]])]});
            extrude(context, id + "F17", {"entities" : qUnion([Q0, Q1, Q2]), "operationType" : NewBodyOperationType.ADD, "depth" : 3 * mm});
        }
    });
